# Revit family: BC_Hitachi_RPFI-FSN2E-1.0-2.5_LOD200
name_source: partatom
category: Equipement de génie climatique
revit_build: Autodesk Revit 2016 (Build: 20150220_1215(x64)
units: mm (PartAtom-declared; Revit-internal decimal feet)

## family parameters
Basée sur le plan de construction = Non
Cote de connecteur circulaire = Utiliser le diamètre
Couper avec des vides une fois chargée = Non
Numéro OmniClass = 23.75.00.00
Partagée = Non
Point de calcul de pièce = Non
Titre OmniClass = Climate Control (HVAC)
Toujours verticalement = Oui
Type d'élément = Normal

## types (4) — shared parameters
Air outlet = 20.00 mm
Color = Spring white (4.1Y8.5/0.7)
Description = RPFI - FSN2E - Floor concealed type
Electrical box (high) distance = 30.00 mm
Electrical box (low) distance = 30.00 mm
Fabricant = HITACHI
Frequency = 50 Hz
Input Height = 50.00 mm
Maximum AC Voltage = 253 V
Minimum AC Voltage = 207 V
Modèle = RPFI - FSN2E - Floor concealed type
Nominal Voltage = 230 V
Number of Poles = 1
Outlet Diameter = 18.50 mm
Output Height = 122.00 mm
Overall Depth = 220.00 mm
Overall Height = 600.00 mm
Refrigerant = R410A (factory-charged corrosion-proof nitrogen)
Sound power max (dB(A)) = 60
Usage Current = 5 A

## per-type parameters (varying)
| type | Acoustic Pressure Level Maxi (dB) | Acoustic Pressure Level Medium (dB) | Acoustic Pressure Level Mini (dB) | Air flow Speed (high/medium/low) m3/min | Cooling Capacity | Fan motor type (output) | Gas Diameter | Heating Capacity | Input Width | Liquid Diameter | Mass | Maximum Air Flow | Minimum Air Flow | Output Width | Overall Width | Product Code |
| RPFI FSN2E 1.0 | 39 | 36 | 32 | 16/14/11 | 5 kW | 45 W | 12.70 mm | 6 kW | 704.00 mm | 6.35 mm | 27.00 kg | 16000.0 L/min | 11000.0 L/min | 704.00 mm | 754.00 mm | 7E460001 |
| RPFI FSN2E 1.5 | 38 | 35 | 31 | 12/10/9 | 4 kW | 28 W | 12.70 mm | 4 kW | 829.00 mm | 6.35 mm | 23.00 kg | 12000.0 L/min | 9000.0 L/min | 829.00 mm | 879.00 mm | 7E460002 |
| RPFI FSN2E 2.5 | 42 | 38 | 34 | 16/14/11 | 6 kW | 45 W | 15.88 mm | 6 kW | 1079.00 mm | 9.52 mm | 28.00 kg | 16000.0 L/min | 11000.0 L/min | 1079.00 mm | 1129.00 mm | 7E460004 |
| RPFI FSN2E 2.0 | 39 | 36 | 32 | 16/14/11 | 5 kW | 45 W | 15.88 mm | 6 kW | 1079.00 mm | 6.35 mm | 27.00 kg | 16000.0 L/min | 11000.0 L/min | 1079.00 mm | 1129.00 mm | 7E460003 |

note: column(s) folded — value = type name in every type: Commentaires du type

## geometry (parser evidence)
native form markers: Blend x2
no freeform markers — native parametric forms only
